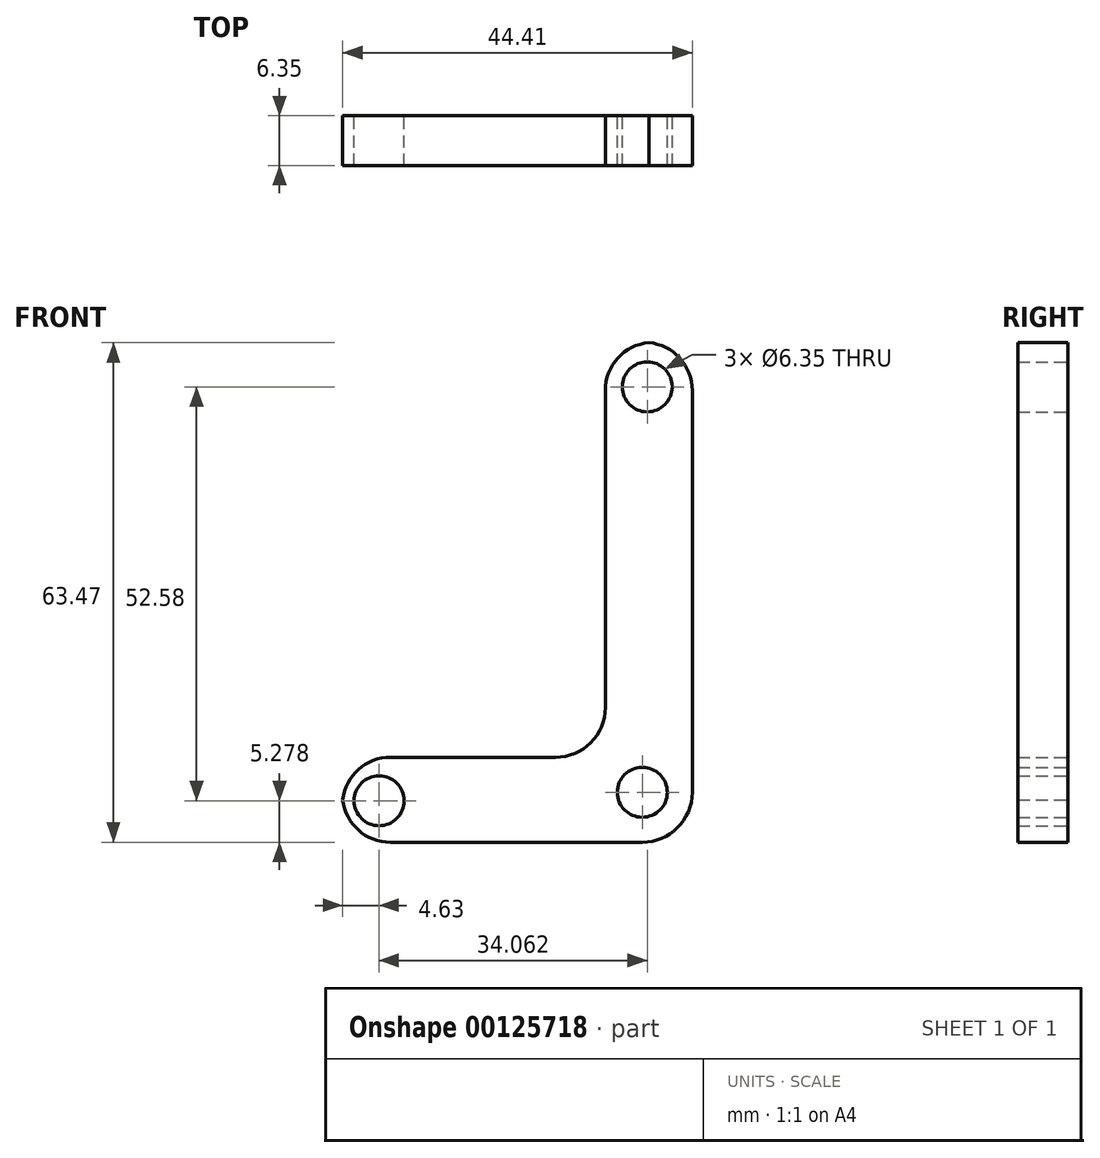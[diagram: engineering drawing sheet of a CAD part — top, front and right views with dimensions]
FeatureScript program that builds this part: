
annotation { "Feature Type Name" : "Feature", "Feature Type Description" : "" }
export const myFeature = defineFeature(function(context is Context, id is Id, definition is map)
    precondition{}
    {
        {
            var Q0;
            Q0=qCreatedBy(makeId("Front.planeOp"),FACE);
            var sketch = newSketch(context, id + "F0", { "sketchPlane" : qUnion([Q0])});
            skLineSegment(sketch, "E0", {"start": v(11.04, 34.45) * mm, "end": v(11.04, -22.7) * mm});
            skLineSegment(sketch, "E1", {"start": v(4.69, -29.05) * mm, "end": v(-33.41, -29.05) * mm});
            skLineSegment(sketch, "E2", {"start": v(-33.41, -29.05) * mm, "end": v(-33.41, -18.26) * mm});
            skLineSegment(sketch, "E3", {"start": v(-33.41, -18.26) * mm, "end": v(-6.35, -18.26) * mm});
            skLineSegment(sketch, "E4", {"start": v(0, -11.91) * mm, "end": v(0, 34.45) * mm});
            skLineSegment(sketch, "E5", {"start": v(0, 34.45) * mm, "end": v(11.04, 34.45) * mm});
            skPoint(sketch, "E6.visualSharp", {"position": v(11.04, -29.05) * mm});
            skArc(sketch, "E6.filletArc", {"start": v(4.69, -29.05) * mm, "mid": v(9.18, -27.2) * mm, "end": v(11.04, -22.7) * mm});
            skPoint(sketch, "E7.visualSharp", {"position": v(0, -18.26) * mm});
            skArc(sketch, "E7.filletArc", {"start": v(-6.35, -18.26) * mm, "mid": v(-1.86, -16.4) * mm, "end": v(0, -11.91) * mm});
            skCircle(sketch, "E8", {"center": v(4.69, -22.7) * mm, "radius": 3.18 * mm});
            skCircle(sketch, "E9", {"center": v(-28.74, -23.77) * mm, "radius": 3.18 * mm});
            skCircle(sketch, "E10", {"center": v(5.32, 28.8) * mm, "radius": 3.18 * mm});
            skSolve(sketch);
        }
        {
            var Q0;
            Q0=makeQuery(id+"F0.imprint","IMPRINT",FACE,{"disambiguationData":[TD([[makeQuery(id+"F0.imprint","IMPRINT",EDGE,{"derivedFrom":sQuery(id+"F0.wireOp",EDGE,"E0")}),-1.0]])]});
            extrude(context, id + "F1", {"entities" : qUnion([Q0]), "depth" : 6.35 * mm});
        }
        {
            var Q0;
            Q0=makeQuery(id+"F1.opExtrude","SWEPT_EDGE",EDGE,{"disambiguationData":[OSD([sQuery(id+"F0.wireOp",EDGE,"E2"),sQuery(id+"F0.wireOp",EDGE,"E3")])]});
            var Q1;
            Q1=makeQuery(id+"F1.opExtrude","SWEPT_EDGE",EDGE,{"disambiguationData":[OSD([sQuery(id+"F0.wireOp",EDGE,"E1"),sQuery(id+"F0.wireOp",EDGE,"E2")])]});
            fillet(context, id + "F2", {"entities" : qUnion([Q0, Q1]), "radius" : 6.1 * mm, "tangentPropagation" : true, "allowEdgeOverflow" : false});
        }
        {
            var Q0;
            Q0=makeQuery(id+"F1.opExtrude","SWEPT_EDGE",EDGE,{"disambiguationData":[OSD([sQuery(id+"F0.wireOp",EDGE,"E4"),sQuery(id+"F0.wireOp",EDGE,"E5")])]});
            var Q1;
            Q1=makeQuery(id+"F1.opExtrude","SWEPT_EDGE",EDGE,{"disambiguationData":[OSD([sQuery(id+"F0.wireOp",EDGE,"E0"),sQuery(id+"F0.wireOp",EDGE,"E5")])]});
            fillet(context, id + "F3", {"entities" : qUnion([Q0, Q1]), "radius" : 6.1 * mm, "tangentPropagation" : true, "allowEdgeOverflow" : false});
        }
    });
